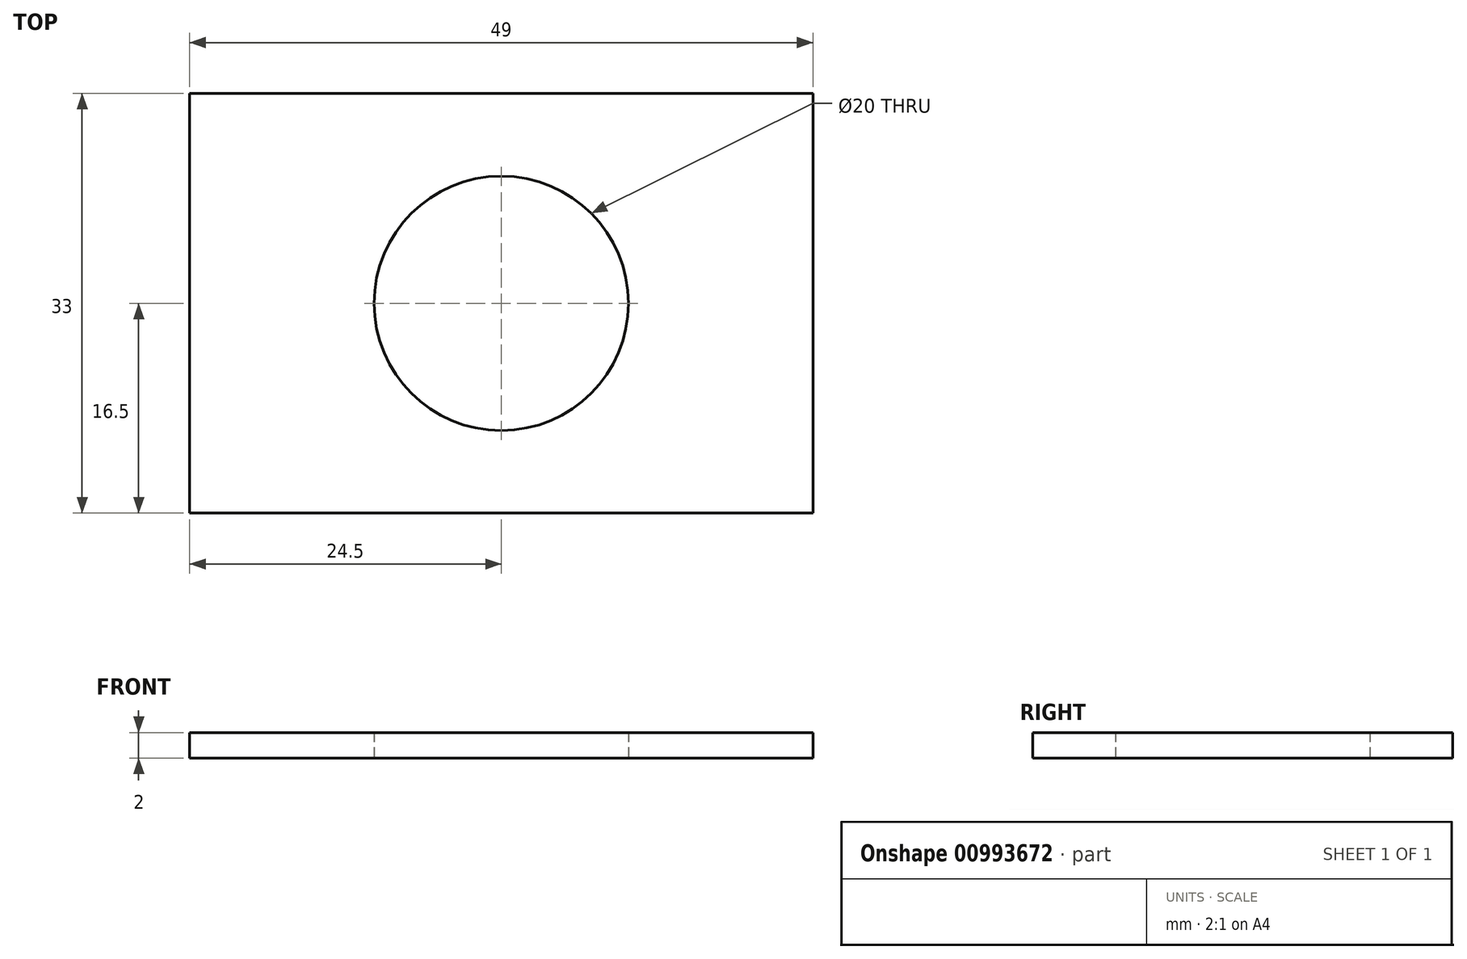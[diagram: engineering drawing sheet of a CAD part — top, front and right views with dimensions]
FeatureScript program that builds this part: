
annotation { "Feature Type Name" : "Feature", "Feature Type Description" : "" }
export const myFeature = defineFeature(function(context is Context, id is Id, definition is map)
    precondition{}
    {
        {
            var Q0;
            Q0=qCreatedBy(makeId("Top.planeOp"),FACE);
            var sketch = newSketch(context, id + "F0", { "sketchPlane" : qUnion([Q0])});
            skLineSegment(sketch, "E0.bottom", {"start": v(-24.5, 16.5) * mm, "end": v(24.5, 16.5) * mm});
            skLineSegment(sketch, "E0.top", {"start": v(-24.5, -16.5) * mm, "end": v(24.5, -16.5) * mm});
            skLineSegment(sketch, "E0.left", {"start": v(-24.5, 16.5) * mm, "end": v(-24.5, -16.5) * mm});
            skLineSegment(sketch, "E0.right", {"start": v(24.5, 16.5) * mm, "end": v(24.5, -16.5) * mm});
            skCircle(sketch, "E1", {"center": v(0, 0) * mm, "radius": 10 * mm});
            skSolve(sketch);
        }
        {
            var Q0;
            Q0=makeQuery(id+"F0.imprint","IMPRINT",FACE,{"disambiguationData":[TD([[makeQuery(id+"F0.imprint","IMPRINT",EDGE,{"derivedFrom":sQuery(id+"F0.wireOp",EDGE,"E0.bottom")}),-1.0]])]});
            extrude(context, id + "F1", {"entities" : qUnion([Q0]), "depth" : 2 * mm, "offsetDistance" : 25 * mm});
        }
    });
